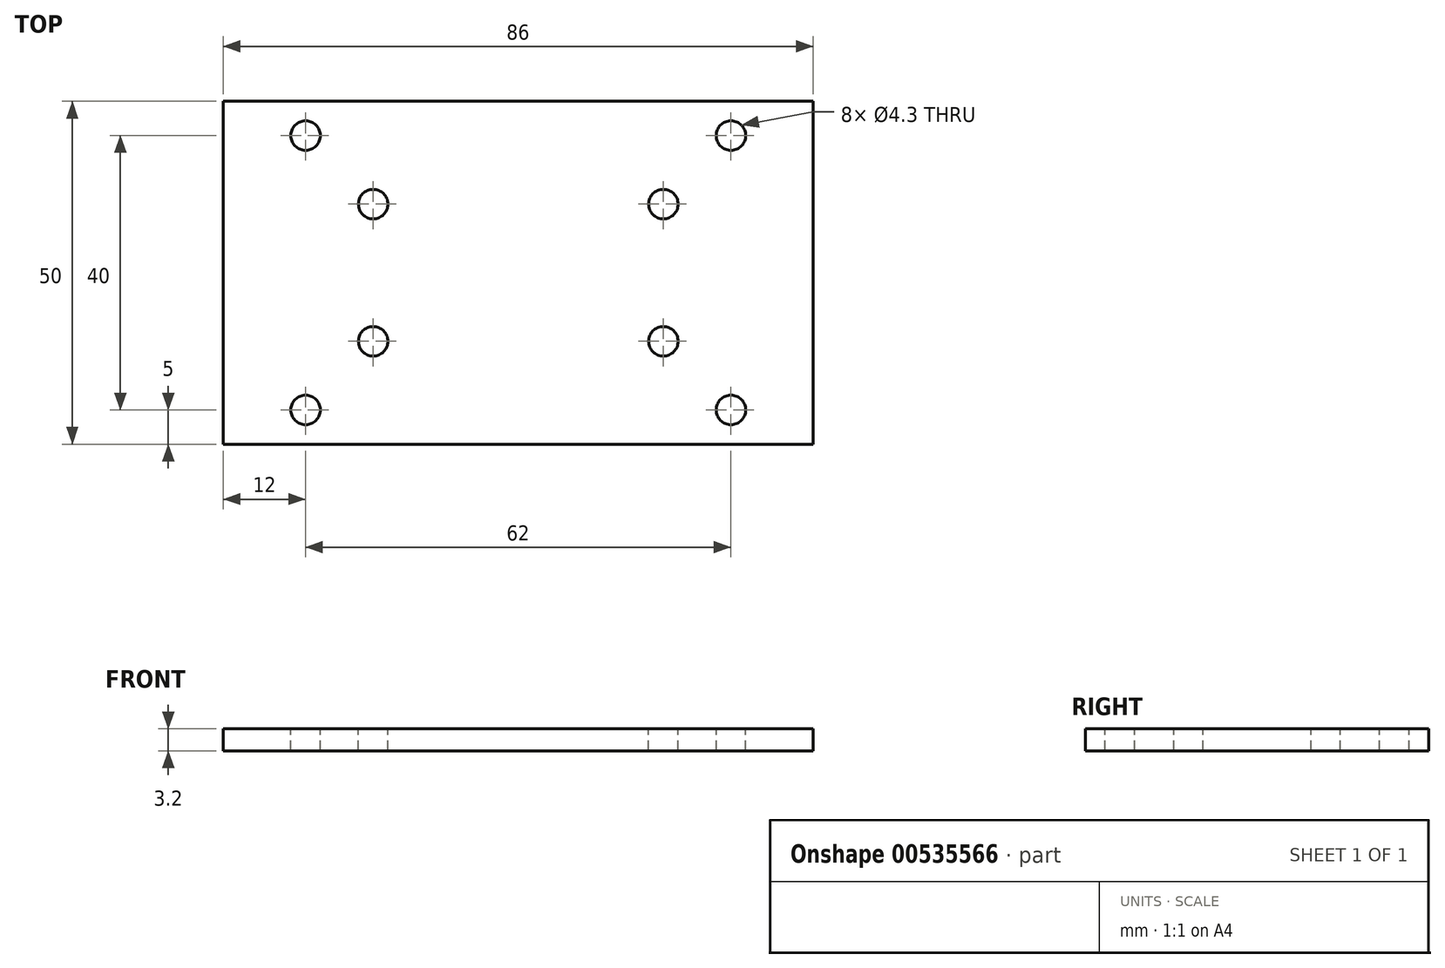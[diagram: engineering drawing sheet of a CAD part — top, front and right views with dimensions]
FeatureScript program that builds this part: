
annotation { "Feature Type Name" : "Feature", "Feature Type Description" : "" }
export const myFeature = defineFeature(function(context is Context, id is Id, definition is map)
    precondition{}
    {
        {
            var Q0;
            Q0=qCreatedBy(makeId("Front.planeOp"),FACE);
            var sketch = newSketch(context, id + "F0", { "sketchPlane" : qUnion([Q0])});
            skLineSegment(sketch, "E0.bottom", {"start": v(-43, 1.6) * mm, "end": v(43, 1.6) * mm});
            skLineSegment(sketch, "E0.top", {"start": v(-43, -1.6) * mm, "end": v(43, -1.6) * mm});
            skLineSegment(sketch, "E0.left", {"start": v(-43, 1.6) * mm, "end": v(-43, -1.6) * mm});
            skLineSegment(sketch, "E0.right", {"start": v(43, 1.6) * mm, "end": v(43, -1.6) * mm});
            skPoint(sketch, "E0.middle", {"position": v(0, 0) * mm});
            skSolve(sketch);
        }
        {
            var Q0;
            Q0 = qSketchRegion(id + "F0", true);
            extrude(context, id + "F1", {"entities" : qUnion([Q0]), "depth" : 50 * mm, "offsetDistance" : 25 * mm, "symmetric" : true});
        }
        {
            var Q0;
            Q0=qCreatedBy(makeId("Top.planeOp"),FACE);
            var sketch = newSketch(context, id + "F2", { "sketchPlane" : qUnion([Q0])});
            skCircle(sketch, "E1", {"center": v(-31, -20) * mm, "radius": 2.15 * mm});
            skCircle(sketch, "E2.MirrorC", {"center": v(31, -20) * mm, "radius": 2.15 * mm});
            skCircle(sketch, "E3.MirrorC", {"center": v(-31, 20) * mm, "radius": 2.15 * mm});
            skCircle(sketch, "E4.MirrorC", {"center": v(31, 20) * mm, "radius": 2.15 * mm});
            skSolve(sketch);
        }
        {
            var Q0;
            Q0 = qSketchRegion(id + "F2", true);
            extrude(context, id + "F3", {"entities" : qUnion([Q0]), "operationType" : NewBodyOperationType.REMOVE, "oppositeDirection" : true, "depth" : 25 * mm, "offsetDistance" : 25 * mm, "symmetric" : true});
        }
        {
            var Q0;
            Q0=qCreatedBy(makeId("Top.planeOp"),FACE);
            var sketch = newSketch(context, id + "F4", { "sketchPlane" : qUnion([Q0])});
            skCircle(sketch, "E5", {"center": v(-21.15, 10) * mm, "radius": 2.15 * mm});
            skCircle(sketch, "E6.MirrorC", {"center": v(-21.15, -10) * mm, "radius": 2.15 * mm});
            skCircle(sketch, "E7.MirrorC", {"center": v(21.15, 10) * mm, "radius": 2.15 * mm});
            skCircle(sketch, "E8.MirrorC", {"center": v(21.15, -10) * mm, "radius": 2.15 * mm});
            skSolve(sketch);
        }
        {
            var Q0;
            Q0 = qSketchRegion(id + "F4", true);
            extrude(context, id + "F5", {"entities" : qUnion([Q0]), "operationType" : NewBodyOperationType.REMOVE, "oppositeDirection" : true, "depth" : 25 * mm, "offsetDistance" : 25 * mm, "symmetric" : true});
        }
    });
